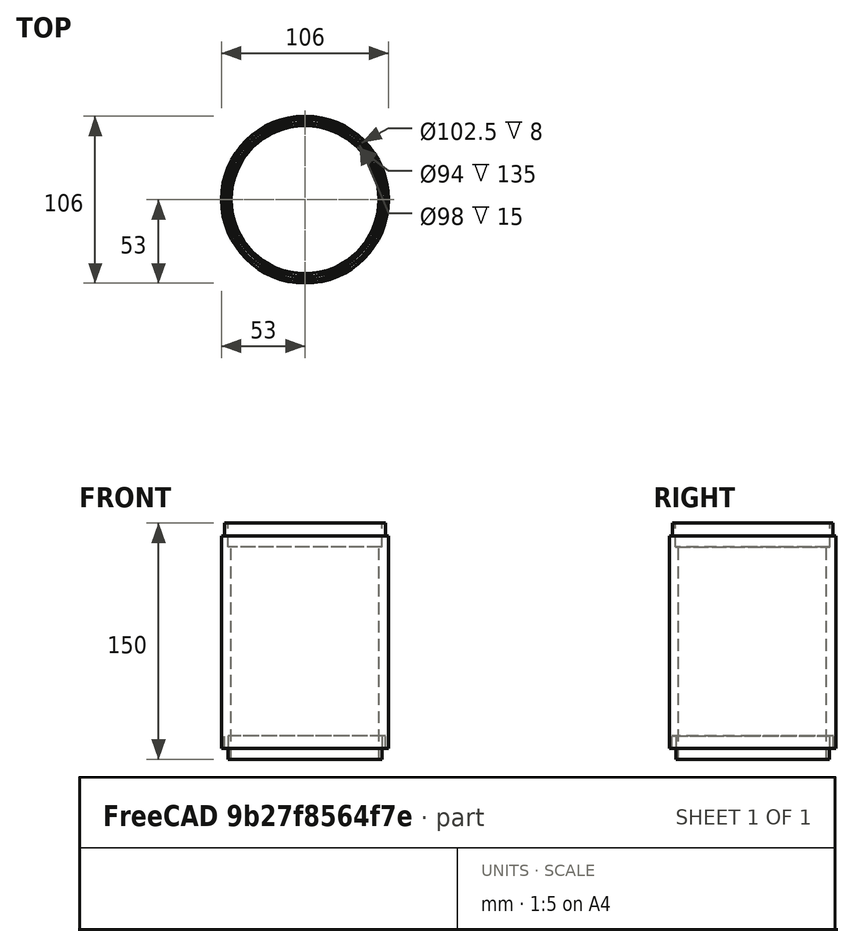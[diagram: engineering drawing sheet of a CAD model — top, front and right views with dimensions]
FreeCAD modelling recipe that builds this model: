
FCSTD DOCUMENT  (FreeCAD 0.20R28720 (Git))
Label: Aeroponics_Modular_4-Tower_Tower-Spacer
License: All rights reserved
LicenseURL: http://en.wikipedia.org/wiki/All_rights_reserved
objects: Sketcher::SketchObject×1, PartDesign::Revolution×1, PartDesign::Body×1
note: 4 computed .brp shape members not serialized (recipe doc carries the construction recipe); baked Part::Feature solids carry a one-line shape summary decoded from their .brp

FEATURE [Sketcher::SketchObject] Sketch
  FullyConstrained = true
  MapMode = 5
  Placement = pos=(0,0,0) rot=(1,0,0;1.5708rad)
  Support = -> [XZ_Plane]
  sketch-geometry (12):
    g0: LineSegment StartX=53 StartY=7 StartZ=0 EndX=51.25 EndY=7 EndZ=0
    g1: LineSegment StartX=51.25 StartY=7 StartZ=0 EndX=51.25 EndY=15 EndZ=0
    g2: LineSegment StartX=51.25 StartY=15 StartZ=0 EndX=48.75 EndY=15 EndZ=0
    g3: LineSegment StartX=48.75 StartY=15 StartZ=0 EndX=48.75 EndY=0 EndZ=0
    g4: LineSegment StartX=48.75 StartY=0 StartZ=0 EndX=47 EndY=0 EndZ=0
    g5: LineSegment StartX=47 StartY=0 StartZ=0 EndX=47 EndY=135 EndZ=0
    g6: LineSegment StartX=47 StartY=135 StartZ=0 EndX=49 EndY=135 EndZ=0
    g7: LineSegment StartX=49 StartY=135 StartZ=0 EndX=49 EndY=150 EndZ=0
    g8: LineSegment StartX=49 StartY=150 StartZ=0 EndX=51 EndY=150 EndZ=0
    g9: LineSegment StartX=51 StartY=150 StartZ=0 EndX=51 EndY=142 EndZ=0
    g10: LineSegment StartX=51 StartY=142 StartZ=0 EndX=53 EndY=142 EndZ=0
    g11: LineSegment StartX=53 StartY=142 StartZ=0 EndX=53 EndY=7 EndZ=0
  constraints (36):
    c: Horizontal(g0)
    c: Coincident(g0,g1)
    c: Vertical(g1)
    c: Coincident(g1,g2)
    c: Horizontal(g2)
    c: Coincident(g2,g3)
    c: PointOnObject(g3,g-1)
    c: Vertical(g3)
    c: Coincident(g3,g4)
    c: Horizontal(g4)
    c: Coincident(g4,g5)
    c: Vertical(g5)
    c: Coincident(g5,g6)
    c: Horizontal(g6)
    c: Coincident(g6,g7)
    c: Vertical(g7)
    c: Coincident(g7,g8)
    c: Horizontal(g8)
    c: Coincident(g8,g9)
    c: Vertical(g9)
    c: Coincident(g9,g10)
    c: Coincident(g10,g11)
    c: Coincident(g11,g0)
    c: Vertical(g11)
    c: DistanceY(g-1,g7) = 150
    c: Equal(g9,g1)
    c: Horizontal(g10)
    c: Equal(g7,g3)
    c: DistanceY(g7,g7) = 15
    c: DistanceY(g9,g9) = 8
    c: DistanceX(g10,g10) = 2
    c: DistanceX(g8,g8) = 2
    c: DistanceX(g6,g6) = 2
    c: DistanceX(g-1,g0) = 53
    c: DistanceX(g2,g2) = 2.5
    c: DistanceX(g4,g4) = 1.75
FEATURE [PartDesign::Revolution] Revolution
  Angle = 360
  Axis = (0,2e-16,1)
  Base = (0,0,0)
  Placement = pos=(0,0,0) rot=(1,0,0;1.5708rad)
  Profile = -> Sketch
  ReferenceAxis = -> Sketch [V_Axis]
  Reversed = true
FEATURE [PartDesign::Body] Body
  Group = -> [Sketch,Revolution]
  Origin = -> Origin
  Tip = -> Revolution
